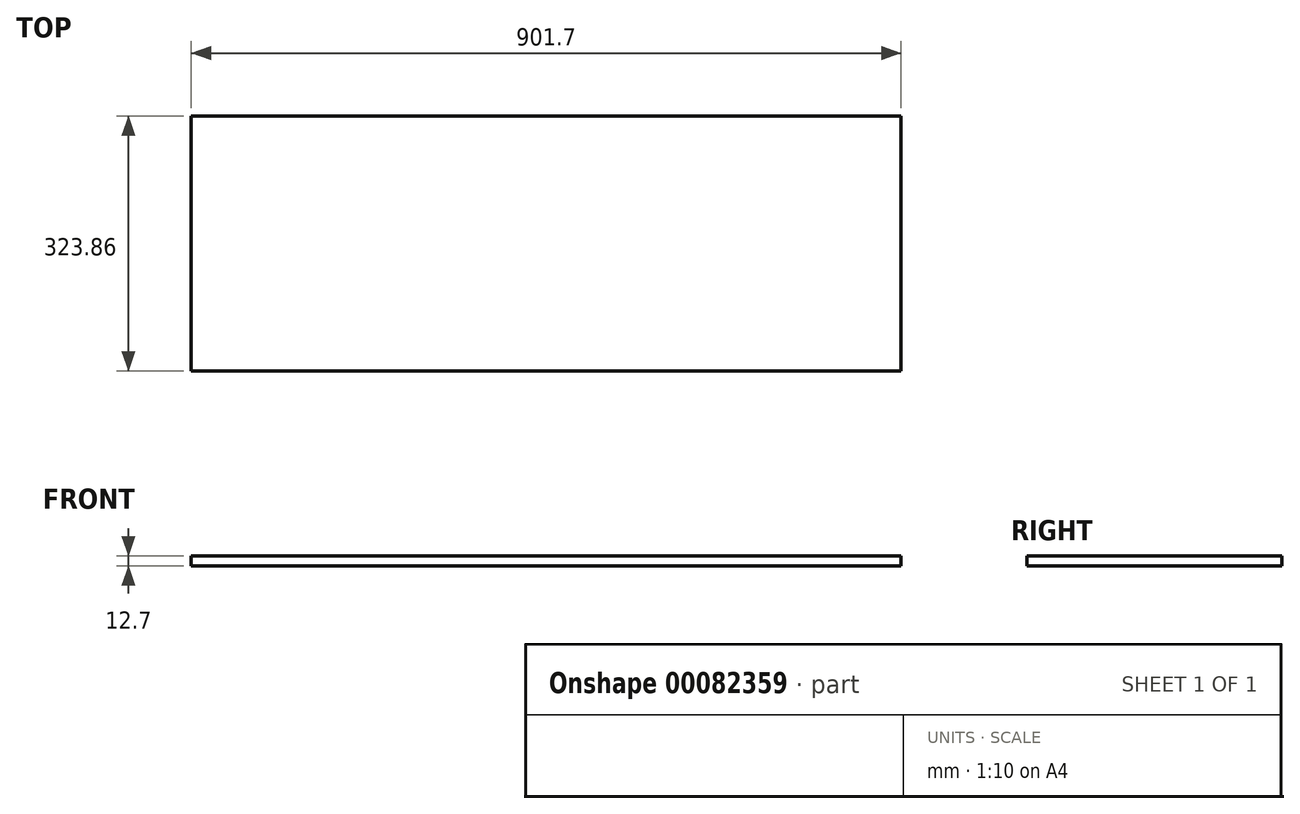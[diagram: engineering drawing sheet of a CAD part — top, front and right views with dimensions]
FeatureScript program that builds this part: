
annotation { "Feature Type Name" : "Feature", "Feature Type Description" : "" }
export const myFeature = defineFeature(function(context is Context, id is Id, definition is map)
    precondition{}
    {
        {
            var Q0;
            Q0=qCreatedBy(makeId("Front.planeOp"),FACE);
            var sketch = newSketch(context, id + "F0", { "sketchPlane" : qUnion([Q0])});
            skLineSegment(sketch, "E0.bottom", {"start": v(450.85, 6.35) * mm, "end": v(-450.85, 6.35) * mm});
            skLineSegment(sketch, "E0.top", {"start": v(450.85, -6.35) * mm, "end": v(-450.85, -6.35) * mm});
            skLineSegment(sketch, "E0.left", {"start": v(450.85, 6.35) * mm, "end": v(450.85, -6.35) * mm});
            skLineSegment(sketch, "E0.right", {"start": v(-450.85, 6.35) * mm, "end": v(-450.85, -6.35) * mm});
            skPoint(sketch, "E0.middle", {"position": v(0, 0) * mm});
            skSolve(sketch);
        }
        {
            var Q0;
            Q0 = qSketchRegion(id + "F0", true);
            extrude(context, id + "F1", {"entities" : qUnion([Q0]), "depth" : 323.85 * mm, "symmetric" : true});
        }
    });
